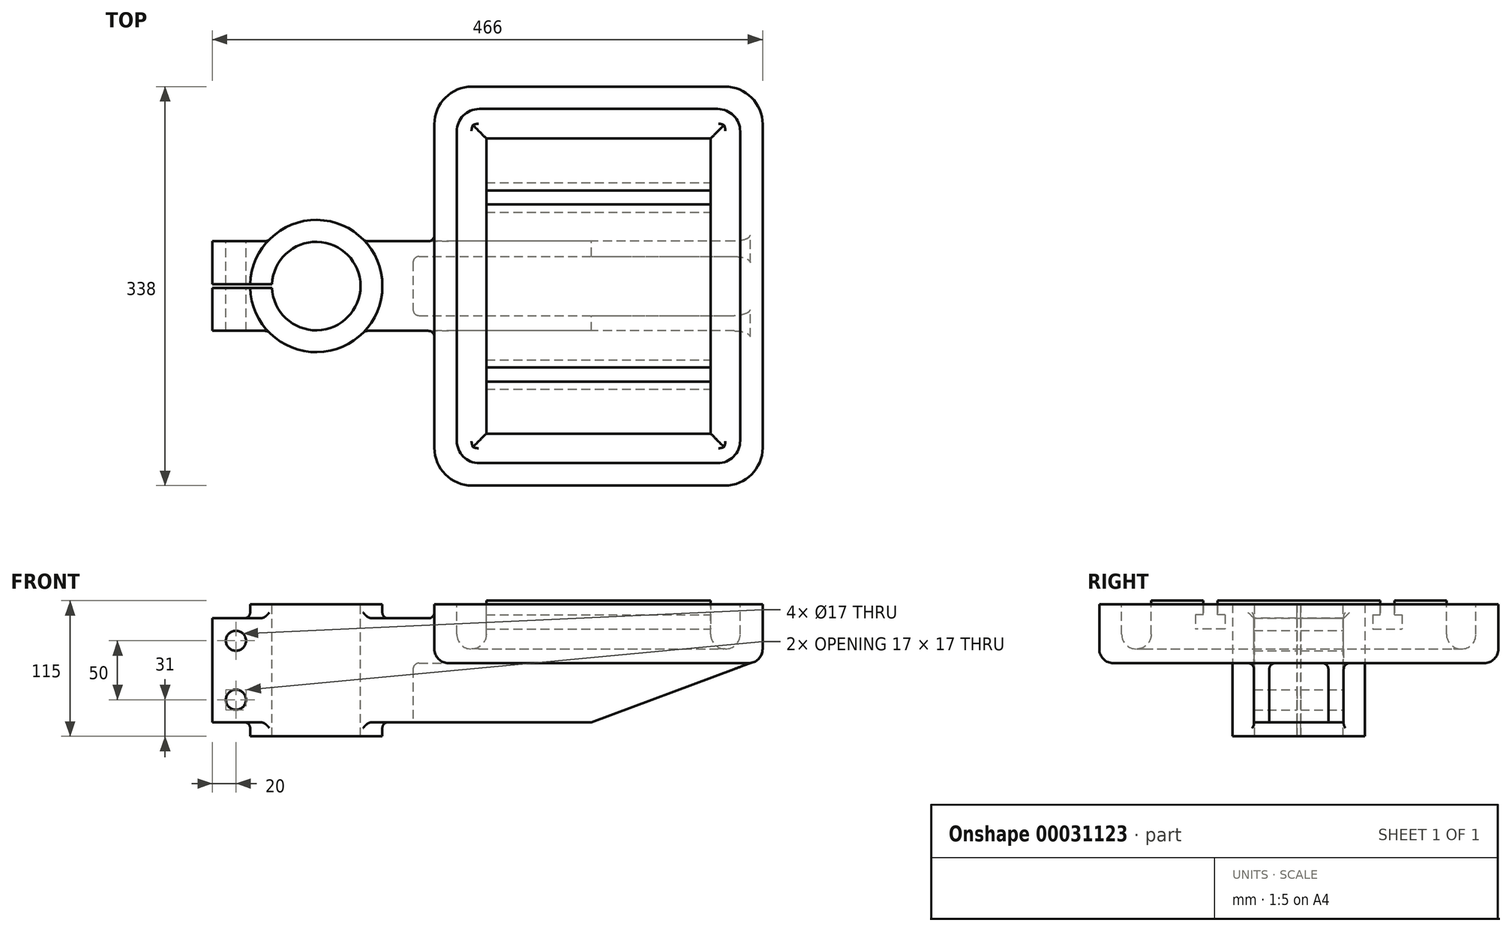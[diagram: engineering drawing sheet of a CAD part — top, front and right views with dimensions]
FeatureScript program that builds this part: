
annotation { "Feature Type Name" : "Feature", "Feature Type Description" : "" }
export const myFeature = defineFeature(function(context is Context, id is Id, definition is map)
    precondition{}
    {
        {
            var Q0;
            Q0=qCreatedBy(makeId("Top.planeOp"),FACE);
            var sketch = newSketch(context, id + "F0", { "sketchPlane" : qUnion([Q0])});
            skCircle(sketch, "E0", {"center": v(0, 0) * mm, "radius": 56 * mm});
            skSolve(sketch);
        }
        {
            var Q0;
            Q0 = qSketchRegion(id + "F0", true);
            extrude(context, id + "F1", {"entities" : qUnion([Q0]), "endBound" : BoundingType.SYMMETRIC, "depth" : 112 * mm});
        }
        {
            var Q0;
            Q0=qCreatedBy(makeId("Front.planeOp"),FACE);
            var sketch = newSketch(context, id + "F2", { "sketchPlane" : qUnion([Q0])});
            skLineSegment(sketch, "E1", {"start": v(-88, 44) * mm, "end": v(0, 44) * mm});
            skLineSegment(sketch, "E2", {"start": v(0, 44) * mm, "end": v(378, 44) * mm});
            skLineSegment(sketch, "E3", {"start": v(378, 44) * mm, "end": v(378, 10) * mm});
            skLineSegment(sketch, "E4", {"start": v(378, 10) * mm, "end": v(233, -44) * mm});
            skLineSegment(sketch, "E5", {"start": v(233, -44) * mm, "end": v(0, -44) * mm});
            skLineSegment(sketch, "E6", {"start": v(0, -44) * mm, "end": v(-88, -44) * mm});
            skLineSegment(sketch, "E7", {"start": v(-88, -44) * mm, "end": v(-88, 44) * mm});
            skCircle(sketch, "E8", {"center": v(-68, 25) * mm, "radius": 8.5 * mm});
            skCircle(sketch, "E9", {"center": v(-68, -25) * mm, "radius": 8.5 * mm});
            skLineSegment(sketch, "E10", {"start": v(-88, 0) * mm, "end": v(0, 0) * mm, "construction": true});
            skLineSegment(sketch, "E11", {"start": v(100, 56) * mm, "end": v(100, 10) * mm, "construction": true});
            skLineSegment(sketch, "E12", {"start": v(100, 10) * mm, "end": v(378, 10) * mm, "construction": true});
            skLineSegment(sketch, "E13", {"start": v(378, 10) * mm, "end": v(378, 56) * mm, "construction": true});
            skLineSegment(sketch, "E14", {"start": v(378, 56) * mm, "end": v(100, 56) * mm, "construction": true});
            skSolve(sketch);
        }
        {
            var Q0;
            Q0=makeQuery(id+"F2.imprint","IMPRINT",FACE,{"disambiguationData":[TD([[makeQuery(id+"F2.imprint","IMPRINT",EDGE,{"derivedFrom":sQuery(id+"F2.wireOp",EDGE,"E1")}),-1.0]])]});
            extrude(context, id + "F3", {"entities" : qUnion([Q0]), "operationType" : NewBodyOperationType.ADD, "endBound" : BoundingType.SYMMETRIC, "depth" : 76 * mm});
        }
        {
            var Q0;
            {var subQ0=sQuery(id+"F2.wireOp",EDGE,"E5");var subQ1=sQuery(id+"F2.wireOp",EDGE,"E6");var subQ2=sQuery(id+"F2.wireOp",EDGE,"E4");Q0=makeQuery(id+"F3.boolean.opBoolean","SPLIT",FACE,{"disambiguationData":[TD([makeQuery(id+"F3.opExtrude","SWEPT_FACE",FACE,{"disambiguationData":[OSD([subQ2])]})])],"derivedFrom":makeQuery(id+"F3.opExtrude","SWEPT_FACE",FACE,{"disambiguationData":[OSD([subQ0,subQ1])]})});}
            var sketch = newSketch(context, id + "F4", { "sketchPlane" : qUnion([Q0])});
            skLineSegment(sketch, "E15.rect.bottom", {"start": v(87, -25) * mm, "end": v(453.32, -25) * mm});
            skLineSegment(sketch, "E15.rect.top", {"start": v(87, 25) * mm, "end": v(453.32, 25) * mm});
            skLineSegment(sketch, "E15.rect.left", {"start": v(82, -20) * mm, "end": v(82, 20) * mm});
            skLineSegment(sketch, "E15.rect.right", {"start": v(453.32, -25) * mm, "end": v(453.32, 25) * mm});
            skPoint(sketch, "E15.rect.middle", {"position": v(267.66, 0) * mm});
            skPoint(sketch, "E16.visualSharp", {"position": v(82, 25) * mm});
            skArc(sketch, "E16.filletArc", {"start": v(87, 25) * mm, "mid": v(83.46, 23.54) * mm, "end": v(82, 20) * mm});
            skPoint(sketch, "E17.visualSharp", {"position": v(82, -25) * mm});
            skArc(sketch, "E17.filletArc", {"start": v(82, -20) * mm, "mid": v(83.46, -23.54) * mm, "end": v(87, -25) * mm});
            skSolve(sketch);
        }
        {
            var Q0;
            Q0 = qSketchRegion(id + "F4", true);
            extrude(context, id + "F5", {"entities" : qUnion([Q0]), "operationType" : NewBodyOperationType.REMOVE, "oppositeDirection" : true, "depth" : 50 * mm});
        }
        {
            var Q0;
            Q0=makeQuery(id+"F3.boolean.opBoolean","INTERSECT",EDGE,{"disambiguationData":[OD(0.0)],"derivedFrom":[makeQuery(id+"F1.opExtrude","SWEPT_FACE",FACE,{"disambiguationData":[OSD([sQuery(id+"F0.wireOp",EDGE,"E0")])]}),makeQuery(id+"F3.opExtrude","CAP_FACE",FACE,{"disambiguationData":[OSD([sQuery(id+"F2.wireOp",EDGE,"E1"),sQuery(id+"F2.wireOp",EDGE,"E2"),sQuery(id+"F2.wireOp",EDGE,"E3"),sQuery(id+"F2.wireOp",EDGE,"E4"),sQuery(id+"F2.wireOp",EDGE,"E5"),sQuery(id+"F2.wireOp",EDGE,"E6"),sQuery(id+"F2.wireOp",EDGE,"E7"),sQuery(id+"F2.wireOp",EDGE,"E8"),sQuery(id+"F2.wireOp",EDGE,"E9")])],"isStart":false})]});
            var Q1;
            Q1=makeQuery(id+"F3.boolean.opBoolean","INTERSECT",EDGE,{"disambiguationData":[OD(1.0)],"derivedFrom":[makeQuery(id+"F1.opExtrude","SWEPT_FACE",FACE,{"disambiguationData":[OSD([sQuery(id+"F0.wireOp",EDGE,"E0")])]}),makeQuery(id+"F3.opExtrude","CAP_FACE",FACE,{"disambiguationData":[OSD([sQuery(id+"F2.wireOp",EDGE,"E1"),sQuery(id+"F2.wireOp",EDGE,"E2"),sQuery(id+"F2.wireOp",EDGE,"E3"),sQuery(id+"F2.wireOp",EDGE,"E4"),sQuery(id+"F2.wireOp",EDGE,"E5"),sQuery(id+"F2.wireOp",EDGE,"E6"),sQuery(id+"F2.wireOp",EDGE,"E7"),sQuery(id+"F2.wireOp",EDGE,"E8"),sQuery(id+"F2.wireOp",EDGE,"E9")])],"isStart":false})]});
            var Q2;
            Q2=makeQuery(id+"F3.boolean.opBoolean","INTERSECT",EDGE,{"disambiguationData":[OD(1.0)],"derivedFrom":[makeQuery(id+"F1.opExtrude","SWEPT_FACE",FACE,{"disambiguationData":[OSD([sQuery(id+"F0.wireOp",EDGE,"E0")])]}),makeQuery(id+"F3.opExtrude","SWEPT_FACE",FACE,{"disambiguationData":[OSD([sQuery(id+"F2.wireOp",EDGE,"E1"),sQuery(id+"F2.wireOp",EDGE,"E2")])]})]});
            var Q3;
            Q3=makeQuery(id+"F3.boolean.opBoolean","INTERSECT",EDGE,{"disambiguationData":[OD(0.0)],"derivedFrom":[makeQuery(id+"F1.opExtrude","SWEPT_FACE",FACE,{"disambiguationData":[OSD([sQuery(id+"F0.wireOp",EDGE,"E0")])]}),makeQuery(id+"F3.opExtrude","SWEPT_FACE",FACE,{"disambiguationData":[OSD([sQuery(id+"F2.wireOp",EDGE,"E1"),sQuery(id+"F2.wireOp",EDGE,"E2")])]})]});
            var Q4;
            Q4=makeQuery(id+"F3.boolean.opBoolean","INTERSECT",EDGE,{"disambiguationData":[OD(1.0)],"derivedFrom":[makeQuery(id+"F1.opExtrude","SWEPT_FACE",FACE,{"disambiguationData":[OSD([sQuery(id+"F0.wireOp",EDGE,"E0")])]}),makeQuery(id+"F3.opExtrude","CAP_FACE",FACE,{"disambiguationData":[OSD([sQuery(id+"F2.wireOp",EDGE,"E1"),sQuery(id+"F2.wireOp",EDGE,"E2"),sQuery(id+"F2.wireOp",EDGE,"E3"),sQuery(id+"F2.wireOp",EDGE,"E4"),sQuery(id+"F2.wireOp",EDGE,"E5"),sQuery(id+"F2.wireOp",EDGE,"E6"),sQuery(id+"F2.wireOp",EDGE,"E7"),sQuery(id+"F2.wireOp",EDGE,"E8"),sQuery(id+"F2.wireOp",EDGE,"E9")])],"isStart":true})]});
            var Q5;
            Q5=makeQuery(id+"F3.boolean.opBoolean","INTERSECT",EDGE,{"disambiguationData":[OD(0.0)],"derivedFrom":[makeQuery(id+"F1.opExtrude","SWEPT_FACE",FACE,{"disambiguationData":[OSD([sQuery(id+"F0.wireOp",EDGE,"E0")])]}),makeQuery(id+"F3.opExtrude","CAP_FACE",FACE,{"disambiguationData":[OSD([sQuery(id+"F2.wireOp",EDGE,"E1"),sQuery(id+"F2.wireOp",EDGE,"E2"),sQuery(id+"F2.wireOp",EDGE,"E3"),sQuery(id+"F2.wireOp",EDGE,"E4"),sQuery(id+"F2.wireOp",EDGE,"E5"),sQuery(id+"F2.wireOp",EDGE,"E6"),sQuery(id+"F2.wireOp",EDGE,"E7"),sQuery(id+"F2.wireOp",EDGE,"E8"),sQuery(id+"F2.wireOp",EDGE,"E9")])],"isStart":true})]});
            var Q6;
            Q6=makeQuery(id+"F3.boolean.opBoolean","INTERSECT",EDGE,{"disambiguationData":[OD(0.0)],"derivedFrom":[makeQuery(id+"F1.opExtrude","SWEPT_FACE",FACE,{"disambiguationData":[OSD([sQuery(id+"F0.wireOp",EDGE,"E0")])]}),makeQuery(id+"F3.opExtrude","SWEPT_FACE",FACE,{"disambiguationData":[OSD([sQuery(id+"F2.wireOp",EDGE,"E5"),sQuery(id+"F2.wireOp",EDGE,"E6")])]})]});
            var Q7;
            Q7=makeQuery(id+"F3.boolean.opBoolean","INTERSECT",EDGE,{"disambiguationData":[OD(1.0)],"derivedFrom":[makeQuery(id+"F1.opExtrude","SWEPT_FACE",FACE,{"disambiguationData":[OSD([sQuery(id+"F0.wireOp",EDGE,"E0")])]}),makeQuery(id+"F3.opExtrude","SWEPT_FACE",FACE,{"disambiguationData":[OSD([sQuery(id+"F2.wireOp",EDGE,"E5"),sQuery(id+"F2.wireOp",EDGE,"E6")])]})]});
            fillet(context, id + "F6", {"entities" : qUnion([Q0, Q1, Q2, Q3, Q4, Q5, Q6, Q7]), "radius" : 5 * mm, "tangentPropagation" : true, "allowEdgeOverflow" : false});
        }
        {
            var Q0;
            Q0=makeQuery(id+"F1.opExtrude","CAP_FACE",FACE,{"disambiguationData":[OSD([sQuery(id+"F0.wireOp",EDGE,"E0")])],"isStart":false});
            var sketch = newSketch(context, id + "F7", { "sketchPlane" : qUnion([Q0])});
            skLineSegment(sketch, "E18.rect.bottom", {"start": v(132, -169) * mm, "end": v(346, -169) * mm});
            skLineSegment(sketch, "E18.rect.top", {"start": v(132, 169) * mm, "end": v(346, 169) * mm});
            skLineSegment(sketch, "E18.rect.left", {"start": v(100, -137) * mm, "end": v(100, 137) * mm});
            skLineSegment(sketch, "E18.rect.right", {"start": v(378, -137) * mm, "end": v(378, 137) * mm});
            skPoint(sketch, "E18.rect.middle", {"position": v(239, 0) * mm});
            skPoint(sketch, "E19.visualSharp", {"position": v(100, 169) * mm});
            skArc(sketch, "E19.filletArc", {"start": v(132, 169) * mm, "mid": v(109.37, 159.63) * mm, "end": v(100, 137) * mm});
            skPoint(sketch, "E20.visualSharp", {"position": v(100, -169) * mm});
            skArc(sketch, "E20.filletArc", {"start": v(100, -137) * mm, "mid": v(109.37, -159.63) * mm, "end": v(132, -169) * mm});
            skPoint(sketch, "E21.visualSharp", {"position": v(378, -169) * mm});
            skArc(sketch, "E21.filletArc", {"start": v(346, -169) * mm, "mid": v(368.63, -159.63) * mm, "end": v(378, -137) * mm});
            skPoint(sketch, "E22.visualSharp", {"position": v(378, 169) * mm});
            skArc(sketch, "E22.filletArc", {"start": v(378, 137) * mm, "mid": v(368.63, 159.63) * mm, "end": v(346, 169) * mm});
            skLineSegment(sketch, "E23.rect.bottom", {"start": v(138, -150) * mm, "end": v(340, -150) * mm});
            skLineSegment(sketch, "E23.rect.top", {"start": v(138, 150) * mm, "end": v(340, 150) * mm});
            skLineSegment(sketch, "E23.rect.left", {"start": v(119, -131) * mm, "end": v(119, 131) * mm});
            skLineSegment(sketch, "E23.rect.right", {"start": v(359, -131) * mm, "end": v(359, 131) * mm});
            skPoint(sketch, "E24.visualSharp", {"position": v(119, 150) * mm});
            skArc(sketch, "E24.filletArc", {"start": v(138, 150) * mm, "mid": v(124.56, 144.44) * mm, "end": v(119, 131) * mm});
            skPoint(sketch, "E25.visualSharp", {"position": v(119, -150) * mm});
            skArc(sketch, "E25.filletArc", {"start": v(119, -131) * mm, "mid": v(124.56, -144.44) * mm, "end": v(138, -150) * mm});
            skPoint(sketch, "E26.visualSharp", {"position": v(359, -150) * mm});
            skArc(sketch, "E26.filletArc", {"start": v(340, -150) * mm, "mid": v(353.44, -144.44) * mm, "end": v(359, -131) * mm});
            skPoint(sketch, "E27.visualSharp", {"position": v(359, 150) * mm});
            skArc(sketch, "E27.filletArc", {"start": v(359, 131) * mm, "mid": v(353.44, 144.44) * mm, "end": v(340, 150) * mm});
            skLineSegment(sketch, "E28.rect.bottom", {"start": v(144, -125) * mm, "end": v(334, -125) * mm});
            skLineSegment(sketch, "E28.rect.top", {"start": v(144, 125) * mm, "end": v(334, 125) * mm});
            skLineSegment(sketch, "E28.rect.left", {"start": v(144, -125) * mm, "end": v(144, 125) * mm});
            skLineSegment(sketch, "E28.rect.right", {"start": v(334, -125) * mm, "end": v(334, 125) * mm});
            skSolve(sketch);
        }
        {
            var Q0;
            Q0=makeQuery(id+"F7.imprint","IMPRINT",FACE,{"disambiguationData":[TD([[makeQuery(id+"F7.imprint","IMPRINT",EDGE,{"derivedFrom":sQuery(id+"F7.wireOp",EDGE,"E18.rect.bottom")}),1.0]])]});
            var Q1;
            Q1=makeQuery(id+"F7.imprint","IMPRINT",FACE,{"disambiguationData":[TD([[makeQuery(id+"F7.imprint","IMPRINT",EDGE,{"derivedFrom":sQuery(id+"F7.wireOp",EDGE,"E23.rect.bottom")}),1.0]])]});
            var Q2;
            Q2=makeQuery(id+"F7.imprint","IMPRINT",FACE,{"disambiguationData":[TD([[makeQuery(id+"F7.imprint","IMPRINT",EDGE,{"derivedFrom":sQuery(id+"F7.wireOp",EDGE,"E28.rect.bottom")}),1.0]])]});
            extrude(context, id + "F8", {"entities" : qUnion([Q0, Q1, Q2]), "operationType" : NewBodyOperationType.ADD, "oppositeDirection" : true, "depth" : 50 * mm});
        }
        {
            var Q0;
            Q0=makeQuery(id+"F7.imprint","IMPRINT",FACE,{"disambiguationData":[TD([[makeQuery(id+"F7.imprint","IMPRINT",EDGE,{"derivedFrom":sQuery(id+"F7.wireOp",EDGE,"E23.rect.bottom")}),1.0]])]});
            extrude(context, id + "F9", {"entities" : qUnion([Q0]), "operationType" : NewBodyOperationType.REMOVE, "oppositeDirection" : true, "depth" : 38 * mm});
        }
        {
            var Q0;
            Q0=makeQuery(id+"F7.imprint","IMPRINT",FACE,{"disambiguationData":[TD([[makeQuery(id+"F7.imprint","IMPRINT",EDGE,{"derivedFrom":sQuery(id+"F7.wireOp",EDGE,"E28.rect.bottom")}),1.0]])]});
            extrude(context, id + "F10", {"entities" : qUnion([Q0]), "operationType" : NewBodyOperationType.ADD, "depth" : 3 * mm});
        }
        {
            var Q0;
            Q0=makeQuery(id+"F9.boolean.opBoolean","COPY",FACE,{"derivedFrom":makeQuery(id+"F9.opExtrude","CAP_FACE",FACE,{"disambiguationData":[OSD([sQuery(id+"F7.wireOp",EDGE,"E23.rect.bottom"),sQuery(id+"F7.wireOp",EDGE,"E23.rect.top"),sQuery(id+"F7.wireOp",EDGE,"E23.rect.left"),sQuery(id+"F7.wireOp",EDGE,"E23.rect.right"),sQuery(id+"F7.wireOp",EDGE,"E24.filletArc"),sQuery(id+"F7.wireOp",EDGE,"E25.filletArc"),sQuery(id+"F7.wireOp",EDGE,"E26.filletArc"),sQuery(id+"F7.wireOp",EDGE,"E27.filletArc"),sQuery(id+"F7.wireOp",EDGE,"E28.rect.bottom"),sQuery(id+"F7.wireOp",EDGE,"E28.rect.top"),sQuery(id+"F7.wireOp",EDGE,"E28.rect.left"),sQuery(id+"F7.wireOp",EDGE,"E28.rect.right")])],"isStart":false})});
            fillet(context, id + "F11", {"entities" : qUnion([Q0]), "radius" : 12.5 * mm, "tangentPropagation" : true, "allowEdgeOverflow" : false});
        }
        {
            var Q0;
            Q0=makeQuery(id+"F8.opExtrude","CAP_EDGE",EDGE,{"disambiguationData":[OSD([sQuery(id+"F7.wireOp",EDGE,"E18.rect.bottom")])],"isStart":false});
            var Q1;
            Q1=makeQuery(id+"F8.opExtrude","CAP_EDGE",EDGE,{"disambiguationData":[OSD([sQuery(id+"F7.wireOp",EDGE,"E18.rect.top")])],"isStart":false});
            var Q2;
            {var subQ0=sQuery(id+"F2.wireOp",EDGE,"E3");var subQ1=sQuery(id+"F2.wireOp",EDGE,"E4");var subQ2=sQuery(id+"F4.wireOp",EDGE,"E15.rect.top");var subQ3=sQuery(id+"F4.wireOp",EDGE,"E15.rect.bottom");Q2=makeQuery(id+"F5.boolean.opBoolean","SPLIT",EDGE,{"disambiguationData":[TD([makeQuery(id+"F3.opExtrude","SWEPT_FACE",FACE,{"disambiguationData":[OSD([subQ0])]}),makeQuery(id+"F3.opExtrude","SWEPT_FACE",FACE,{"disambiguationData":[OSD([subQ1])]}),makeQuery(id+"F5.opExtrude","SWEPT_FACE",FACE,{"disambiguationData":[OSD([subQ3])]}),makeQuery(id+"F5.opExtrude","CAP_FACE",FACE,{"disambiguationData":[OSD([subQ3,subQ2,sQuery(id+"F4.wireOp",EDGE,"E15.rect.left"),sQuery(id+"F4.wireOp",EDGE,"E15.rect.right"),sQuery(id+"F4.wireOp",EDGE,"E16.filletArc"),sQuery(id+"F4.wireOp",EDGE,"E17.filletArc")])],"isStart":false}),makeQuery(id+"F5.opExtrude","SWEPT_FACE",FACE,{"disambiguationData":[OSD([subQ2])]})])],"derivedFrom":makeQuery(id+"F3.opExtrude","SWEPT_EDGE",EDGE,{"disambiguationData":[OSD([subQ0,subQ1])]})});}
            fillet(context, id + "F12", {"entities" : qUnion([Q0, Q1, Q2]), "radius" : 12 * mm, "tangentPropagation" : true, "allowEdgeOverflow" : false});
        }
        {
            var Q0;
            {var subQ0=sQuery(id+"F2.wireOp",EDGE,"E1");var subQ1=sQuery(id+"F2.wireOp",EDGE,"E2");var subQ2=sQuery(id+"F2.wireOp",EDGE,"E3");var subQ3=sQuery(id+"F2.wireOp",EDGE,"E4");var subQ4=sQuery(id+"F2.wireOp",EDGE,"E5");var subQ5=sQuery(id+"F2.wireOp",EDGE,"E6");Q0=makeQuery(id+"F8.boolean.opBoolean","INTERSECT",EDGE,{"derivedFrom":[makeQuery(id+"F3.boolean.opBoolean","SPLIT",FACE,{"disambiguationData":[TD([makeQuery(id+"F3.opExtrude","SWEPT_FACE",FACE,{"disambiguationData":[OSD([subQ2])]})])],"derivedFrom":makeQuery(id+"F3.opExtrude","CAP_FACE",FACE,{"disambiguationData":[OSD([subQ0,subQ1,subQ2,subQ3,subQ4,subQ5,sQuery(id+"F2.wireOp",EDGE,"E7"),sQuery(id+"F2.wireOp",EDGE,"E8"),sQuery(id+"F2.wireOp",EDGE,"E9")])],"isStart":false})}),makeQuery(id+"F8.opExtrude","CAP_FACE",FACE,{"disambiguationData":[OSD([sQuery(id+"F7.wireOp",EDGE,"E18.rect.bottom"),sQuery(id+"F7.wireOp",EDGE,"E18.rect.top"),sQuery(id+"F7.wireOp",EDGE,"E18.rect.left"),sQuery(id+"F7.wireOp",EDGE,"E18.rect.right"),sQuery(id+"F7.wireOp",EDGE,"E19.filletArc"),sQuery(id+"F7.wireOp",EDGE,"E20.filletArc"),sQuery(id+"F7.wireOp",EDGE,"E21.filletArc"),sQuery(id+"F7.wireOp",EDGE,"E22.filletArc")])],"isStart":false})]});}
            var Q1;
            Q1=makeQuery(id+"F5.boolean.opBoolean","COPY",EDGE,{"derivedFrom":makeQuery(id+"F5.opExtrude","CAP_EDGE",EDGE,{"disambiguationData":[OSD([sQuery(id+"F4.wireOp",EDGE,"E15.rect.top")])],"isStart":false})});
            var Q2;
            {var subQ0=sQuery(id+"F2.wireOp",EDGE,"E1");var subQ1=sQuery(id+"F2.wireOp",EDGE,"E2");var subQ2=sQuery(id+"F2.wireOp",EDGE,"E3");var subQ3=sQuery(id+"F2.wireOp",EDGE,"E4");var subQ4=sQuery(id+"F2.wireOp",EDGE,"E5");var subQ5=sQuery(id+"F2.wireOp",EDGE,"E6");Q2=makeQuery(id+"F8.boolean.opBoolean","INTERSECT",EDGE,{"derivedFrom":[makeQuery(id+"F3.boolean.opBoolean","SPLIT",FACE,{"disambiguationData":[TD([makeQuery(id+"F3.opExtrude","SWEPT_FACE",FACE,{"disambiguationData":[OSD([subQ2])]})])],"derivedFrom":makeQuery(id+"F3.opExtrude","CAP_FACE",FACE,{"disambiguationData":[OSD([subQ0,subQ1,subQ2,subQ3,subQ4,subQ5,sQuery(id+"F2.wireOp",EDGE,"E7"),sQuery(id+"F2.wireOp",EDGE,"E8"),sQuery(id+"F2.wireOp",EDGE,"E9")])],"isStart":true})}),makeQuery(id+"F8.opExtrude","CAP_FACE",FACE,{"disambiguationData":[OSD([sQuery(id+"F7.wireOp",EDGE,"E18.rect.bottom"),sQuery(id+"F7.wireOp",EDGE,"E18.rect.top"),sQuery(id+"F7.wireOp",EDGE,"E18.rect.left"),sQuery(id+"F7.wireOp",EDGE,"E18.rect.right"),sQuery(id+"F7.wireOp",EDGE,"E19.filletArc"),sQuery(id+"F7.wireOp",EDGE,"E20.filletArc"),sQuery(id+"F7.wireOp",EDGE,"E21.filletArc"),sQuery(id+"F7.wireOp",EDGE,"E22.filletArc")])],"isStart":false})]});}
            fillet(context, id + "F13", {"entities" : qUnion([Q0, Q1, Q2]), "radius" : 5 * mm, "tangentPropagation" : true, "allowEdgeOverflow" : false});
        }
        {
            var Q0;
            Q0=makeQuery(id+"F1.opExtrude","CAP_FACE",FACE,{"disambiguationData":[OSD([sQuery(id+"F0.wireOp",EDGE,"E0")])],"isStart":false});
            var sketch = newSketch(context, id + "F14", { "sketchPlane" : qUnion([Q0])});
            skArc(sketch, "E29", {"start": v(-37.47, -1.5) * mm, "mid": v(37.5, 0) * mm, "end": v(-37.47, 1.5) * mm});
            skLineSegment(sketch, "E30.bottom", {"start": v(-37.47, -1.5) * mm, "end": v(-96.27, -1.5) * mm});
            skLineSegment(sketch, "E30.top", {"start": v(-37.47, 1.5) * mm, "end": v(-96.27, 1.5) * mm});
            skLineSegment(sketch, "E30.right", {"start": v(-96.27, -1.5) * mm, "end": v(-96.27, 1.5) * mm});
            skLineSegment(sketch, "E31", {"start": v(0, 0) * mm, "end": v(-37.47, 0) * mm, "construction": true});
            skSolve(sketch);
        }
        {
            var Q0;
            Q0 = qSketchRegion(id + "F14", true);
            extrude(context, id + "F15", {"entities" : qUnion([Q0]), "operationType" : NewBodyOperationType.REMOVE, "endBound" : BoundingType.THROUGH_ALL, "oppositeDirection" : true, "depth" : 25 * mm});
        }
        {
            var Q0;
            {var subQ0=sQuery(id+"F7.wireOp",EDGE,"E28.rect.right");Q0=makeQuery(id+"F10.boolean.opBoolean","MERGE",FACE,{"derivedFrom":[makeQuery(id+"F9.boolean.opBoolean","COPY",FACE,{"derivedFrom":makeQuery(id+"F9.opExtrude","SWEPT_FACE",FACE,{"disambiguationData":[OSD([subQ0])]})}),makeQuery(id+"F10.opExtrude","SWEPT_FACE",FACE,{"disambiguationData":[OSD([subQ0])]})]});}
            var sketch = newSketch(context, id + "F16", { "sketchPlane" : qUnion([Q0])});
            skLineSegment(sketch, "E32.bottom", {"start": v(81, 59) * mm, "end": v(69, 59.1) * mm});
            skLineSegment(sketch, "E32.left", {"start": v(81, 59) * mm, "end": v(81, 47) * mm});
            skLineSegment(sketch, "E32.right", {"start": v(69, 59.1) * mm, "end": v(69, 47) * mm});
            skLineSegment(sketch, "E33.bottom", {"start": v(62.5, 47) * mm, "end": v(69, 47) * mm});
            skLineSegment(sketch, "E33.top", {"start": v(62.5, 35) * mm, "end": v(87.5, 35) * mm});
            skLineSegment(sketch, "E33.left", {"start": v(62.5, 47) * mm, "end": v(62.5, 35) * mm});
            skLineSegment(sketch, "E33.right", {"start": v(87.5, 47) * mm, "end": v(87.5, 35) * mm});
            skLineSegment(sketch, "E34.trimOffspring", {"start": v(81, 47) * mm, "end": v(87.5, 47) * mm});
            skLineSegment(sketch, "E35", {"start": v(75, 59.05) * mm, "end": v(75, 35) * mm, "construction": true});
            skLineSegment(sketch, "E36", {"start": v(0, 0) * mm, "end": v(0, 93.23) * mm, "construction": true});
            skLineSegment(sketch, "E37.MirrorCS", {"start": v(-62.5, 47) * mm, "end": v(-62.5, 35) * mm});
            skLineSegment(sketch, "E38.MirrorCS", {"start": v(-62.5, 35) * mm, "end": v(-87.5, 35) * mm});
            skLineSegment(sketch, "E39.MirrorCS", {"start": v(-87.5, 47) * mm, "end": v(-87.5, 35) * mm});
            skLineSegment(sketch, "E40.MirrorCS", {"start": v(-81, 59) * mm, "end": v(-81, 47) * mm});
            skLineSegment(sketch, "E41.MirrorCS", {"start": v(-81, 47) * mm, "end": v(-87.5, 47) * mm});
            skLineSegment(sketch, "E42.MirrorCS", {"start": v(-62.5, 47) * mm, "end": v(-69, 47) * mm});
            skLineSegment(sketch, "E43.MirrorCS", {"start": v(-81, 59) * mm, "end": v(-69, 59.1) * mm});
            skLineSegment(sketch, "E44", {"start": v(-69, 59.1) * mm, "end": v(-69, 47) * mm});
            skSolve(sketch);
        }
        {
            var Q0;
            Q0 = qSketchRegion(id + "F16", true);
            extrude(context, id + "F17", {"entities" : qUnion([Q0]), "operationType" : NewBodyOperationType.REMOVE, "endBound" : BoundingType.UP_TO_NEXT, "oppositeDirection" : true, "depth" : 25 * mm});
        }
        {
            var Q0;
            {var subQ0=sQuery(id+"F2.wireOp",EDGE,"E1");var subQ1=sQuery(id+"F2.wireOp",EDGE,"E2");var subQ2=sQuery(id+"F2.wireOp",EDGE,"E3");Q0=makeQuery(id+"F8.boolean.opBoolean","INTERSECT",EDGE,{"derivedFrom":[makeQuery(id+"F3.boolean.opBoolean","SPLIT",FACE,{"disambiguationData":[TD([makeQuery(id+"F3.opExtrude","SWEPT_FACE",FACE,{"disambiguationData":[OSD([subQ2])]})])],"derivedFrom":makeQuery(id+"F3.opExtrude","SWEPT_FACE",FACE,{"disambiguationData":[OSD([subQ0,subQ1])]})}),makeQuery(id+"F8.opExtrude","SWEPT_FACE",FACE,{"disambiguationData":[OSD([sQuery(id+"F7.wireOp",EDGE,"E18.rect.left")])]})]});}
            fillet(context, id + "F18", {"entities" : qUnion([Q0]), "radius" : 5 * mm, "tangentPropagation" : true, "allowEdgeOverflow" : false});
        }
    });
